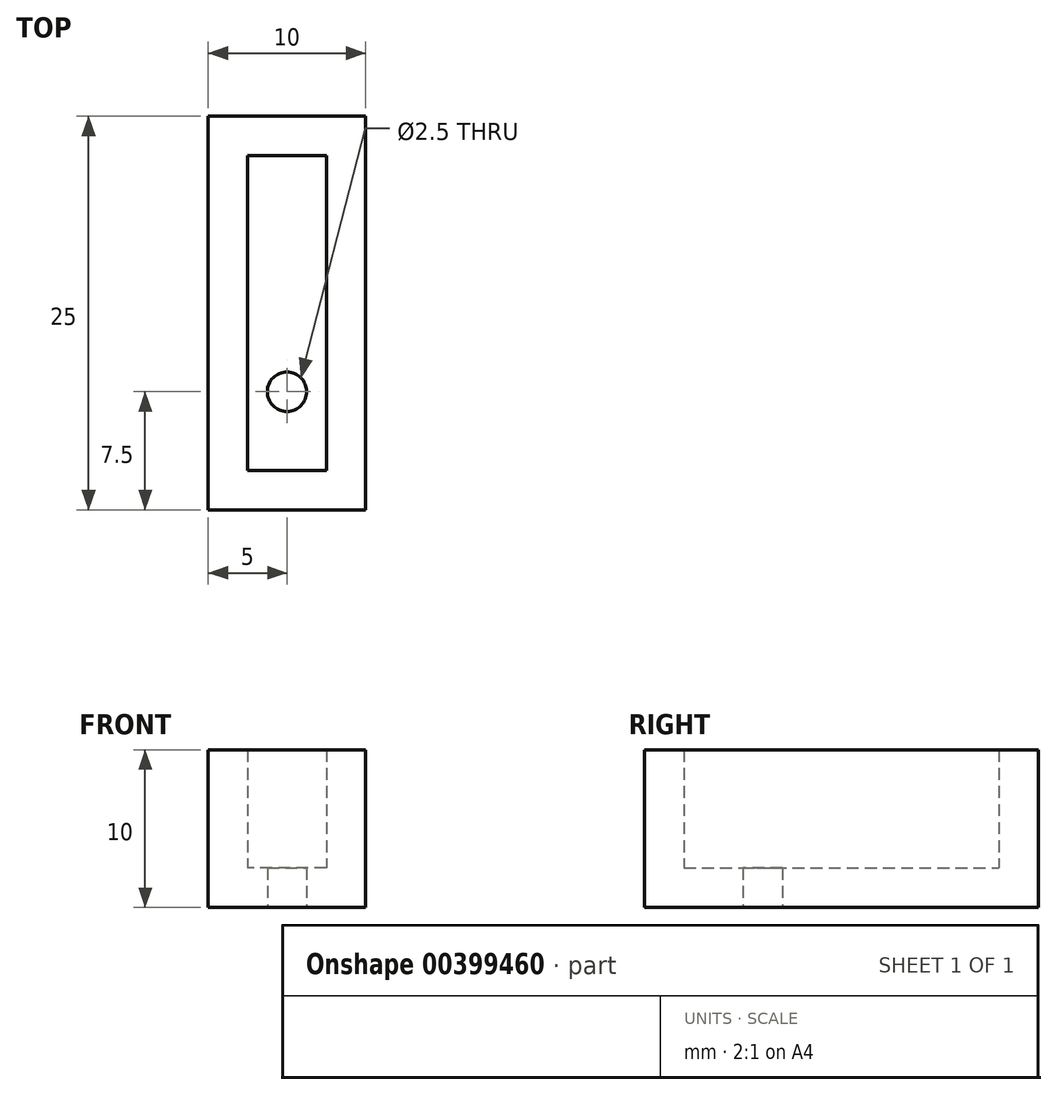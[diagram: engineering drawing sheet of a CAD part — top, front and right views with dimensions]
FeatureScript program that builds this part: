
annotation { "Feature Type Name" : "Feature", "Feature Type Description" : "" }
export const myFeature = defineFeature(function(context is Context, id is Id, definition is map)
    precondition{}
    {
        {
            var Q0;
            Q0=qCreatedBy(makeId("Front.planeOp"),FACE);
            var sketch = newSketch(context, id + "F0", { "sketchPlane" : qUnion([Q0])});
            skLineSegment(sketch, "E0.bottom", {"start": v(5, 5) * mm, "end": v(-5, 5) * mm});
            skLineSegment(sketch, "E0.top", {"start": v(5, -5) * mm, "end": v(-5, -5) * mm});
            skLineSegment(sketch, "E0.left", {"start": v(5, 5) * mm, "end": v(5, -5) * mm});
            skLineSegment(sketch, "E0.right", {"start": v(-5, 5) * mm, "end": v(-5, -5) * mm});
            skPoint(sketch, "E0.middle", {"position": v(0, 0) * mm});
            skSolve(sketch);
        }
        {
            var Q0;
            Q0 = qSketchRegion(id + "F0", true);
            extrude(context, id + "F1", {"entities" : qUnion([Q0]), "endBound" : BoundingType.SYMMETRIC, "depth" : 25 * mm});
        }
        {
            var Q0;
            Q0=makeQuery(id+"F1.opExtrude","SWEPT_FACE",FACE,{"disambiguationData":[OSD([sQuery(id+"F0.wireOp",EDGE,"E0.bottom")])]});
            shell(context, id + "F2", {"entities" : qUnion([Q0]), "thickness" : 2.5 * mm});
        }
        {
            var Q0;
            Q0=makeQuery(id+"F1.opExtrude","SWEPT_FACE",FACE,{"disambiguationData":[OSD([sQuery(id+"F0.wireOp",EDGE,"E0.top")])]});
            var sketch = newSketch(context, id + "F3", { "sketchPlane" : qUnion([Q0])});
            skCircle(sketch, "E1", {"center": v(0, 5) * mm, "radius": 1.25 * mm});
            skSolve(sketch);
        }
        {
            var Q0;
            Q0 = qSketchRegion(id + "F3", true);
            extrude(context, id + "F4", {"entities" : qUnion([Q0]), "operationType" : NewBodyOperationType.REMOVE, "endBound" : BoundingType.THROUGH_ALL, "oppositeDirection" : true, "depth" : 25 * mm});
        }
    });
